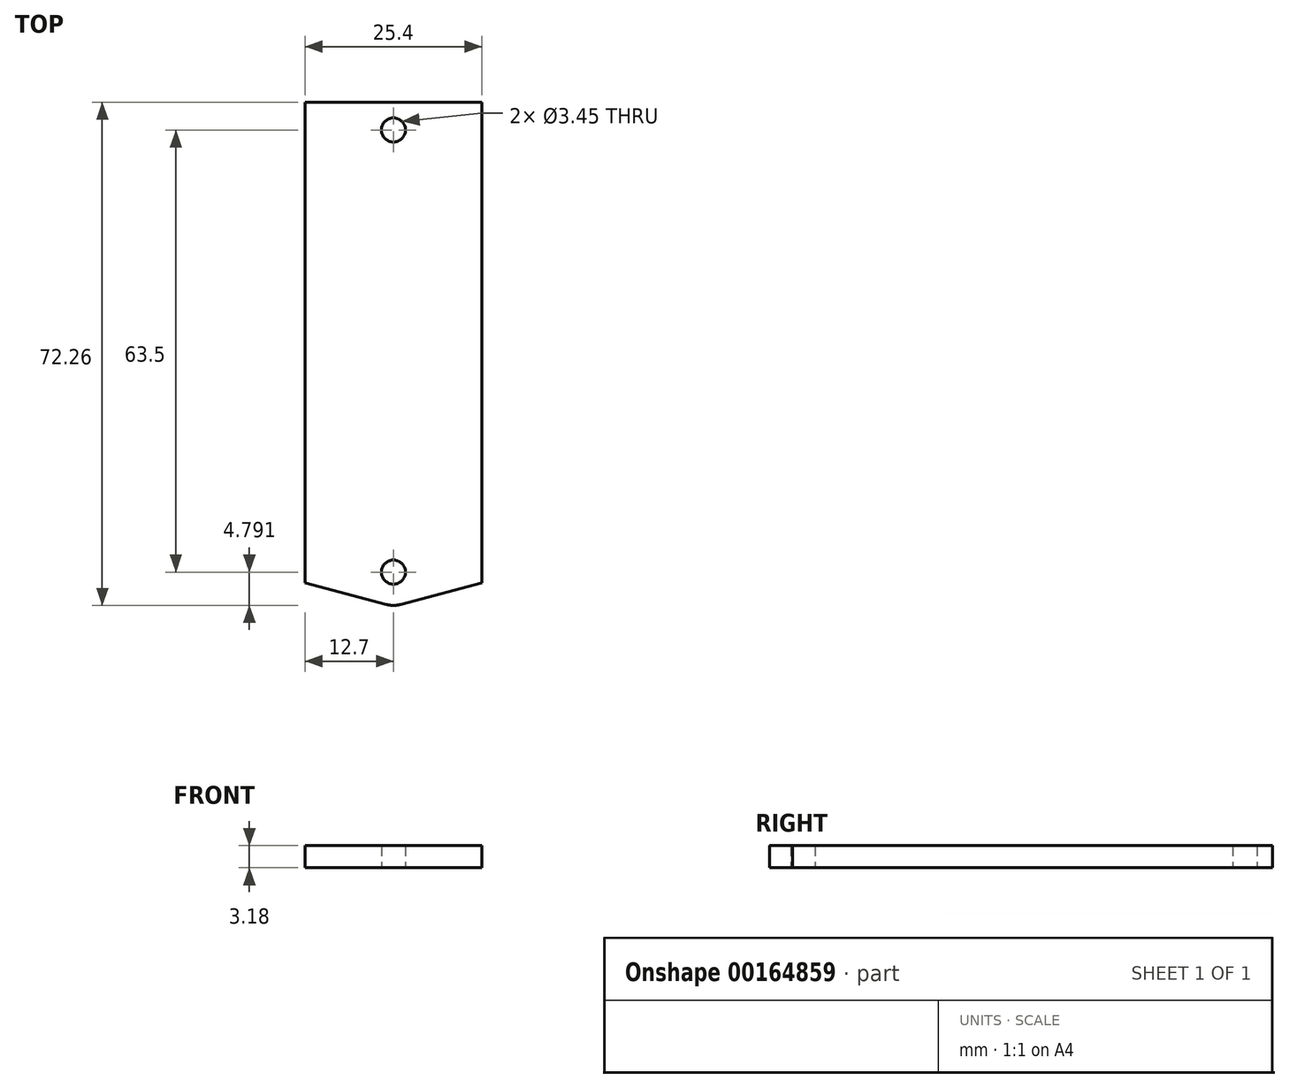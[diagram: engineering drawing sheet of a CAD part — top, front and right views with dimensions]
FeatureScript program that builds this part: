
annotation { "Feature Type Name" : "Feature", "Feature Type Description" : "" }
export const myFeature = defineFeature(function(context is Context, id is Id, definition is map)
    precondition{}
    {
        {
            var Q0;
            Q0=qCreatedBy(makeId("Top.planeOp"),FACE);
            var sketch = newSketch(context, id + "F0", { "sketchPlane" : qUnion([Q0])});
            skLineSegment(sketch, "E0", {"start": v(0, 0) * mm, "end": v(12.7, 3.4) * mm});
            skLineSegment(sketch, "E1", {"start": v(0, 0) * mm, "end": v(-12.7, 3.4) * mm});
            skLineSegment(sketch, "E2", {"start": v(0, 0) * mm, "end": v(0, 4.93) * mm, "construction": true});
            skLineSegment(sketch, "E3", {"start": v(-12.7, 72.4) * mm, "end": v(-12.7, 3.4) * mm});
            skLineSegment(sketch, "E4", {"start": v(12.7, 72.4) * mm, "end": v(12.7, 3.4) * mm});
            skLineSegment(sketch, "E5", {"start": v(0, 4.93) * mm, "end": v(0, 68.43) * mm, "construction": true});
            skCircle(sketch, "E6", {"center": v(0, 4.93) * mm, "radius": 4.76 * mm, "construction": true});
            skLineSegment(sketch, "E7", {"start": v(0, 36.68) * mm, "end": v(12.7, 36.68) * mm, "construction": true});
            skLineSegment(sketch, "E8", {"start": v(0, 36.68) * mm, "end": v(-12.7, 36.68) * mm, "construction": true});
            skCircle(sketch, "E9", {"center": v(0, 68.43) * mm, "radius": 1.73 * mm});
            skCircle(sketch, "E10", {"center": v(0, 4.93) * mm, "radius": 1.73 * mm});
            skLineSegment(sketch, "E11", {"start": v(0, 68.43) * mm, "end": v(0, 72.4) * mm, "construction": true});
            skLineSegment(sketch, "E12", {"start": v(-12.7, 72.4) * mm, "end": v(12.7, 72.4) * mm});
            skSolve(sketch);
        }
        {
            var Q0;
            Q0 = qSketchRegion(id + "F0", true);
            extrude(context, id + "F1", {"entities" : qUnion([Q0]), "depth" : 3.17 * mm});
        }
        {
            var Q0;
            Q0=makeQuery(id+"F1.opExtrude","SWEPT_EDGE",EDGE,{"disambiguationData":[OSD([sQuery(id+"F0.wireOp",EDGE,"E0"),sQuery(id+"F0.wireOp",EDGE,"E1")])]});
            fillet(context, id + "F2", {"entities" : qUnion([Q0]), "radius" : 3.97 * mm, "tangentPropagation" : true, "allowEdgeOverflow" : false});
        }
    });
